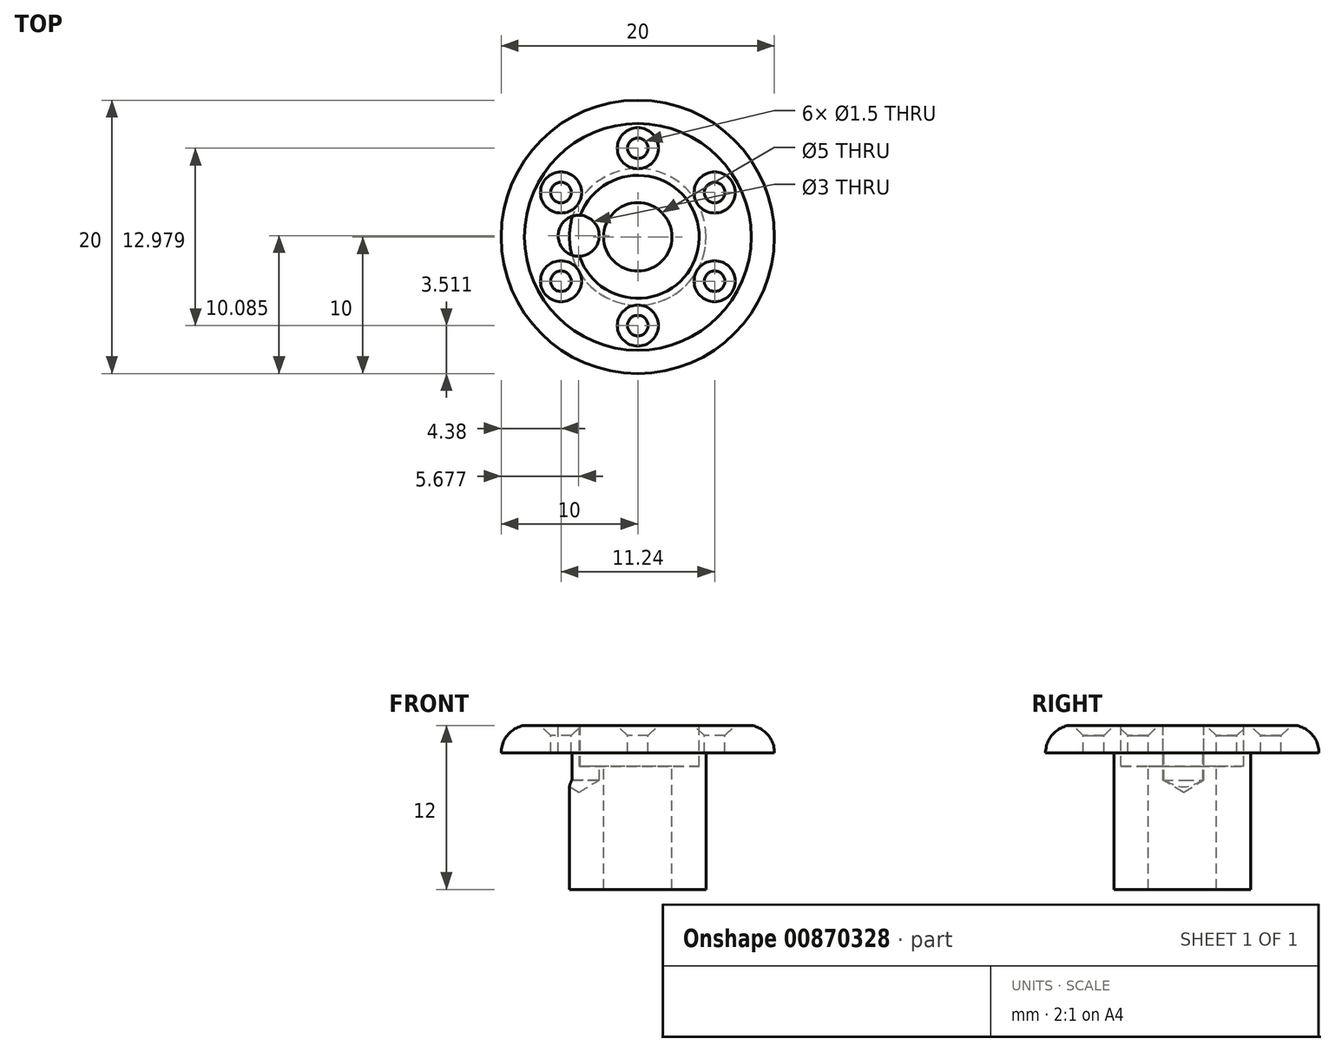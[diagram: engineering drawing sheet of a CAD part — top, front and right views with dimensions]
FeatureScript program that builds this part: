
annotation { "Feature Type Name" : "Feature", "Feature Type Description" : "" }
export const myFeature = defineFeature(function(context is Context, id is Id, definition is map)
    precondition{}
    {
        {
            var Q0;
            Q0=qCreatedBy(makeId("Front.planeOp"),FACE);
            var sketch = newSketch(context, id + "F0", { "sketchPlane" : qUnion([Q0])});
            skLineSegment(sketch, "E0.bottom", {"start": v(-2.5, 4.67) * mm, "end": v(-10, 4.67) * mm});
            skLineSegment(sketch, "E0.top", {"start": v(-2.5, 6.67) * mm, "end": v(-8.3, 6.67) * mm});
            skLineSegment(sketch, "E0.left", {"start": v(-2.5, 4.67) * mm, "end": v(-2.5, 6.67) * mm});
            skLineSegment(sketch, "E1.bottom", {"start": v(-2.5, 4.67) * mm, "end": v(-5, 4.67) * mm});
            skLineSegment(sketch, "E1.top", {"start": v(-2.5, -5.33) * mm, "end": v(-5, -5.33) * mm});
            skLineSegment(sketch, "E1.left", {"start": v(-2.5, 4.67) * mm, "end": v(-2.5, -5.33) * mm});
            skLineSegment(sketch, "E1.right", {"start": v(-5, 4.67) * mm, "end": v(-5, -5.33) * mm});
            skArc(sketch, "E2", {"start": v(-8.3, 6.67) * mm, "mid": v(-9.52, 5.99) * mm, "end": v(-10, 4.67) * mm});
            skPoint(sketch, "E3", {"position": v(-6.25, 6.67) * mm});
            skPoint(sketch, "E0.right.end.orphan", {"position": v(-10, 6.67) * mm});
            skLineSegment(sketch, "E4", {"start": v(0, 12.78) * mm, "end": v(0, -10.28) * mm, "construction": true});
            skSolve(sketch);
        }
        {
            var Q0;
            Q0=makeQuery(id+"F0.imprint","IMPRINT",FACE,{"disambiguationData":[TD([[makeQuery(id+"F0.imprint","IMPRINT",EDGE,{"derivedFrom":sQuery(id+"F0.wireOp",EDGE,"E1.top")}),-1.0]])]});
            var Q1;
            Q1=makeQuery(id+"F0.imprint","IMPRINT",FACE,{"disambiguationData":[TD([[makeQuery(id+"F0.imprint","IMPRINT",EDGE,{"derivedFrom":sQuery(id+"F0.wireOp",EDGE,"E0.top")}),1.0]])]});
            var Q2;
            Q2=sQuery(id+"F0.wireOp",EDGE,"E4");
            revolve(context, id + "F1", {"surfaceOperationType" : NewSurfaceOperationType.NEW, "entities" : qUnion([Q0, Q1]), "axis" : qUnion([Q2]), "revolveType" : RevolveType.FULL});
        }
        {
            var Q0;
            Q0=makeQuery(id+"F1.opRevolve","SWEPT_FACE",FACE,{"disambiguationData":[OSD([sQuery(id+"F0.wireOp",EDGE,"E0.top")])]});
            var sketch = newSketch(context, id + "F2", { "sketchPlane" : qUnion([Q0])});
            skLineSegment(sketch, "E5", {"start": v(0, 11.73) * mm, "end": v(0, -10.9) * mm, "construction": true});
            skCircle(sketch, "E6", {"center": v(0, 0) * mm, "radius": 4.5 * mm});
            skSolve(sketch);
        }
        {
            var Q0;
            Q0=makeQuery(id+"F2.imprint","IMPRINT",FACE,{"disambiguationData":[TD([[makeQuery(id+"F2.imprint","IMPRINT",EDGE,{"derivedFrom":sQuery(id+"F2.wireOp",EDGE,"E6")}),1.0]])]});
            extrude(context, id + "F3", {"entities" : qUnion([Q0]), "operationType" : NewBodyOperationType.REMOVE, "oppositeDirection" : true, "depth" : 3 * mm, "offsetDistance" : 25 * mm});
        }
        {
            var Q0;
            Q0=makeQuery(id+"F1.opRevolve","SWEPT_FACE",FACE,{"disambiguationData":[OSD([sQuery(id+"F0.wireOp",EDGE,"E0.top")])]});
            var sketch = newSketch(context, id + "F4", { "sketchPlane" : qUnion([Q0])});
            skCircle(sketch, "E7.cCircle", {"center": v(0, 0) * mm, "radius": 5.62 * mm, "construction": true});
            skLineSegment(sketch, "E7.0", {"start": v(-5.62, -3.24) * mm, "end": v(-5.62, 3.24) * mm});
            skLineSegment(sketch, "E7.1", {"start": v(-5.62, 3.24) * mm, "end": v(0, 6.49) * mm});
            skLineSegment(sketch, "E7.2", {"start": v(0, 6.49) * mm, "end": v(5.62, 3.24) * mm});
            skLineSegment(sketch, "E7.3", {"start": v(5.62, 3.24) * mm, "end": v(5.62, -3.24) * mm});
            skLineSegment(sketch, "E7.4", {"start": v(5.62, -3.24) * mm, "end": v(0, -6.49) * mm});
            skLineSegment(sketch, "E7.5", {"start": v(0, -6.49) * mm, "end": v(-5.62, -3.24) * mm});
            skPoint(sketch, "E7.0.midPoint", {"position": v(-5.62, 0) * mm});
            skSolve(sketch);
        }
        {
            var Q0;
            Q0=sQuery(id+"F4.wireOp",VERTEX,"E7.1.end");
            var Q1;
            Q1=sQuery(id+"F4.wireOp",VERTEX,"E7.0.end");
            var Q2;
            Q2=sQuery(id+"F4.wireOp",VERTEX,"E7.0.start");
            var Q3;
            Q3=sQuery(id+"F4.wireOp",VERTEX,"E7.4.end");
            var Q4;
            Q4=sQuery(id+"F4.wireOp",VERTEX,"E7.3.end");
            var Q5;
            Q5=sQuery(id+"F4.wireOp",VERTEX,"E7.2.end");
            var Q6;
            Q6=makeQuery(id+"F1.opRevolve","SWEPT_BODY",BODY,{"disambiguationData":[OSD([sQuery(id+"F0.wireOp",EDGE,"E0.bottom"),sQuery(id+"F0.wireOp",EDGE,"E0.top"),sQuery(id+"F0.wireOp",EDGE,"E0.left"),sQuery(id+"F0.wireOp",EDGE,"E1.top"),sQuery(id+"F0.wireOp",EDGE,"E1.left"),sQuery(id+"F0.wireOp",EDGE,"E1.right"),sQuery(id+"F0.wireOp",EDGE,"E2")])]});
            hole(context, id + "F5", {"style" : HoleStyle.C_SINK, "endStyle" : HoleEndStyle.THROUGH, "holeDiameter" : 1.5 * mm, "cSinkDiameter" : 3 * mm, "cSinkAngle" : 90 * degree, "majorDiameter" : 5 * mm, "isTappedThrough" : true, "tappedDepth" : 12 * mm, "tapClearance" : 3, "locations" : qUnion([Q0, Q1, Q2, Q3, Q4, Q5]), "scope" : qUnion([Q6])});
        }
        {
            var Q0;
            Q0=makeQuery(id+"F1.opRevolve","SWEPT_FACE",FACE,{"disambiguationData":[OSD([sQuery(id+"F0.wireOp",EDGE,"E0.top")])]});
            var sketch = newSketch(context, id + "F6", { "sketchPlane" : qUnion([Q0])});
            skCircle(sketch, "E8", {"center": v(-4.32, 0.08) * mm, "radius": 0.97 * mm});
            skPoint(sketch, "E8.first.point", {"position": v(-4.41, -0.88) * mm});
            skPoint(sketch, "E8.second.point", {"position": v(-4.37, 1.05) * mm});
            skPoint(sketch, "E8.third.point", {"position": v(-5.29, 0) * mm});
            skSolve(sketch);
        }
        {
            var Q0;
            Q0=sQuery(id+"F6.wireOp",VERTEX,"E8.center");
            var Q1;
            Q1=makeQuery(id+"F1.opRevolve","SWEPT_BODY",BODY,{"disambiguationData":[OSD([sQuery(id+"F0.wireOp",EDGE,"E0.bottom"),sQuery(id+"F0.wireOp",EDGE,"E0.top"),sQuery(id+"F0.wireOp",EDGE,"E0.left"),sQuery(id+"F0.wireOp",EDGE,"E1.top"),sQuery(id+"F0.wireOp",EDGE,"E1.left"),sQuery(id+"F0.wireOp",EDGE,"E1.right"),sQuery(id+"F0.wireOp",EDGE,"E2")])]});
            hole(context, id + "F7", {"style" : HoleStyle.C_BORE, "endStyle" : HoleEndStyle.BLIND, "holeDiameter" : 3 * mm, "cBoreDiameter" : 3 * mm, "cBoreDepth" : .5 * mm, "majorDiameter" : 5 * mm, "holeDepth" : 1 * mm, "isTappedThrough" : true, "tappedDepth" : 12 * mm, "tapClearance" : 3, "locations" : qUnion([Q0]), "scope" : qUnion([Q1])});
        }
    });
